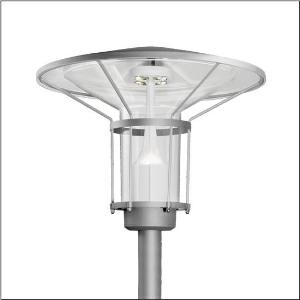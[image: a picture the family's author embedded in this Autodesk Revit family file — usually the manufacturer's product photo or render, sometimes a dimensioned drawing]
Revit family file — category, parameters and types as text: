
# Revit family: laterne_classic_iq___p1_0a_5xa5245ff14hp_7b29
name_source: partatom
category: Lighting Fixtures
units: mm (PartAtom-declared; Revit-internal decimal feet)

## family parameters
Cut with Voids When Loaded = No
Host = Face
Light Source = No
Part Type = Normal
Room Calculation Point = No
Round Connector Dimension = Use Diameter
Shared = No

## types (1)
- --- (1 x LED, 4210 lm, 33.6 W, 3000K)
    Apparent Load = 34 VA
    CIE Flux Codes = 31 61 91 96 100
    Color Rendering = 70
    Color Temperature = 3000K
    Default Elevation = 1800 mm
    Description = Lantern Classic iQ, mast luminaire, Module 540 iQ-SR, primary light control with 3 zone facetted reflector, of plastic, silver coated, highly specular, structured, primary optical cover: cover, of PMMA, transparent, light distribution: P1.0a, light emission: direct distribution, primary light characteristic: strongly asymmetric, installation type: post-top, LED, High Power LED, rated luminous flux: 4.210lm, luminous efficacy: 125lm/W, light colour: 730, colour temperature: 3000K, control gear: ECG iQ, control: pre-setting: logarithmic dimming characteristic, Street-Remote, Auto-Match, Temp-Guard, Lumen-Switch, Night-Set, Smart-Wire, Light-Fading, Desk-Remote (wireless, voltage-free reading and setting of iQ features in the workshop via application-optimized NFC function/RFID function), optimised constant luminous flux control (CLO 2.0), with terminal, 6-pole, max. 2.5mm², mains connection: 230..240V, AC, 50/60Hz, start of lifetime: 34W, end of service life: 36W, reduction: 15W, luminaire housing, upper part, of glass-fibre reinforced polyester, coated, Siteco® metallic grey (DB 702S), diameter: 750mm, height: 596mm, spigot size: d x l = 76 x 70mm (post-top) | with reducer (optional accessory) 60 x 70mm, post-top mast mounting element, of diecast aluminium, coated, Siteco® metallic grey (DB 702S), Module 540 iQ-SR, traffic white (RAL 9016), equipment: Power, protection rating (complete): IP65, insulation class (complete): insulation class II (safety insulation), certification: CE, ENEC, VDE, packaging unit: 1 piece

Light Distribution: P1.0a
    Height = 596 mm
    Lamp = 1 x LED
    Lamp Light Flux = 4210 lm
    Lamp Power = 33.6 W
    Lamp count = 1
    Length = 750 mm
    Luminous efficacy = 125 lm/W
    Manufacturer = Siteco
    ModVariant = No
    Model = 5XA5245FF14HP
    Number of Poles = 1
    OnlyDefault = Yes
    Power Factor = 1
    Product Name = Laterne Classic iQ | P1.0a
    Product group = mast luminaire | pylon top
    ProductGroupID = 6100
    Protection Class = Protection class II
    Protection Degree = IP 65
    RLX_Detail_Level = 1
    RLX_Emergency_Light_Flux = 0 lm
    RLX_Emergency_Type = 0
    RLX_Emergency_Type_DB = No
    RlxData = <blob elided: 65541 chars, md5=3f8af74a>
    Socket = socket
    Standby Power = 0 W
    System Light Flux = 4210 lm
    System Power = 34 W
    Type Comments = factory setting: luminous flux: 100 % | dim-lin: 254 | 695 mA
    Type Image = l_1006052.jpg
    URL = http://relux.com
    VarID = @adj_165849
    Voltage = 0 V
    Weight = 0.00 kg
    Width = 0 mm  [stored 0 ft]

note: [stored X ft] marks values corroborated as IEEE doubles in the binary element streams (Revit-internal decimal feet)

## geometry (parser evidence)
native form markers: Blend x4, Sweep x10
no freeform markers — native parametric forms only
